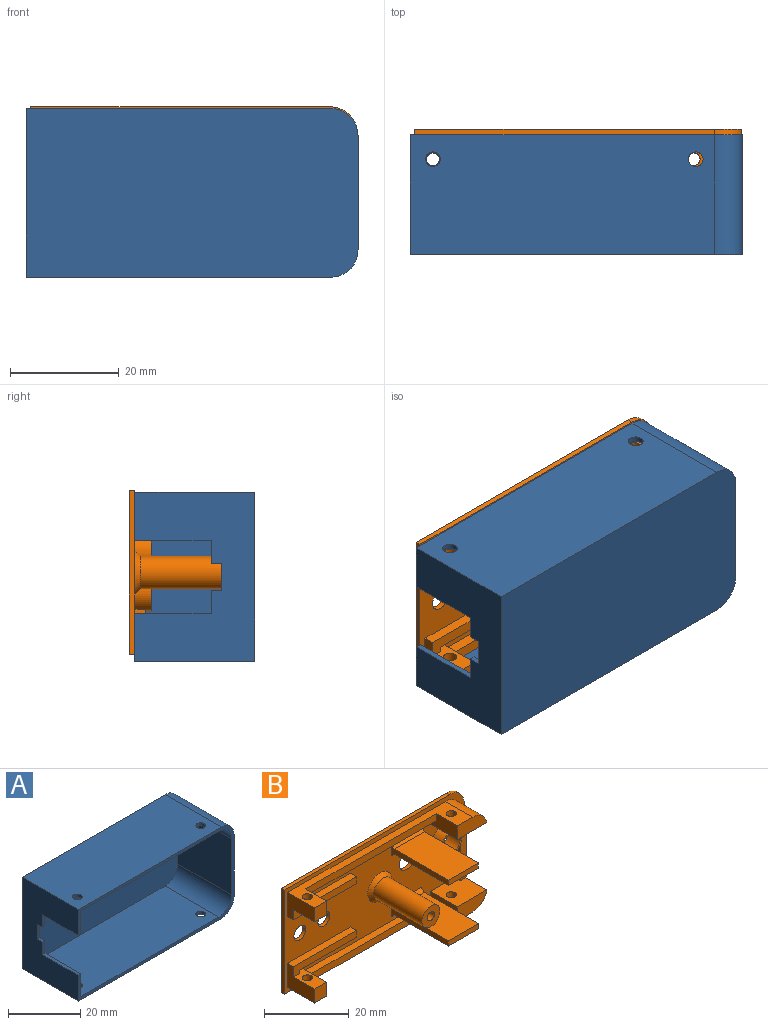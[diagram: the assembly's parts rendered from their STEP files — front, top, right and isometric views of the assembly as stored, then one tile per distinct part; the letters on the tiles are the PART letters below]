
ASSEMBLY  parts=2 mates=1
PART A: 26 faces, bbox 61x22x31 mm
  f0: plane 59x29mm, normal (0,-1,0), area 1700.3mm2, adj f8,f11,f12,f13,f14,f15
  f1: plane 56x22mm, normal (0,0,1), area 1220.5mm2, adj f2,f6,f7,f16,f19,f20
  f2: plane 31x22mm, normal (-1,0,0), area 483mm2, adj f1,f3,f7,f9,f10,f16,f21,f22
  f3: plane 56x22mm, normal (0,0,-1), area 1220.5mm2, adj f2,f4,f7,f16,f17,f18
  f4: cylinder r=5mm len=22mm, axis (0,1,0), area 172.8mm2, adj f3,f5,f7,f16
  f5: plane 22x21mm, normal (1,0,0), area 462mm2, adj f4,f6,f7,f16
  f6: cylinder r=5mm len=22mm, axis (0,1,0), area 172.8mm2, adj f1,f5,f7,f16
  f7: plane 61x31mm, normal (0,1,0), area 1880.3mm2, adj f1,f2,f3,f4,f5,f6
  f8: plane 29x21mm, normal (1,0,0), area 410mm2, adj f0,f9,f10,f11,f15,f16,f21,f22
  f9: plane 14x1mm, normal (0,0,1), area 14mm2, adj f2,f8,f16,f24
  f10: plane 14x1mm, normal (0,0,-1), area 14mm2, adj f2,f8,f16,f22
  f11: plane 54x21mm, normal (0,0,-1), area 1122.5mm2, adj f0,f8,f12,f16,f19,f20
  f12: cylinder r=5mm len=21mm, axis (0,1,0), area 164.9mm2, adj f0,f11,f13,f16
  f13: plane 21x19mm, normal (-1,0,0), area 399mm2, adj f0,f12,f14,f16
  f14: cylinder r=5mm len=21mm, axis (0,1,0), area 164.9mm2, adj f0,f13,f15,f16
  f15: plane 54x21mm, normal (0,0,1), area 1122.5mm2, adj f0,f8,f14,f16,f17,f18
  f16: plane 61x31mm, normal (0,-1,0), area 166.5mm2, adj f1,f2,f3,f4,f5,f6,f8,f9
  f17: cylinder r=1.35mm len=2.7mm, axis (0,0,-1), area 8.5mm2, adj f3,f15
  f18: cylinder r=1.35mm len=2.7mm, axis (0,0,-1), area 8.5mm2, adj f3,f15
  f19: cylinder r=1.35mm len=2.7mm, axis (0,0,-1), area 8.5mm2, adj f1,f11
  f20: cylinder r=1.35mm len=2.7mm, axis (0,0,-1), area 8.5mm2, adj f1,f11
  f21: plane 2x1mm, normal (0,0,-1), area 2mm2, adj f2,f8,f22,f25
  f22: plane 4.25x1mm, normal (0,-1,0), area 4.3mm2, adj f2,f8,f10,f21
  f23: plane 2x1mm, normal (0,0,1), area 2mm2, adj f2,f8,f24,f25
  f24: plane 4.25x1mm, normal (0,-1,0), area 4.3mm2, adj f2,f8,f9,f23
  f25: plane 5x1mm, normal (0,-1,0), area 5mm2, adj f2,f8,f21,f23
PART B: 75 faces, bbox 60x20x30 mm
  f0: plane 9x4mm, normal (1,0,0), area 32mm2, adj f1,f23,f25,f26,f56,f57
  f1: plane 60x30mm, normal (0,-1,0), area 1145.8mm2, adj f0,f2,f3,f4,f5,f6,f7,f8
  f2: plane 9x4mm, normal (0,0,1), area 27.5mm2, adj f1,f20,f21,f22,f52,f55,f69
  f3: plane 9x4mm, normal (-1,0,0), area 32mm2, adj f1,f16,f18,f19,f44,f45
  f4: plane 30x1mm, normal (-1,0,0), area 30mm2, adj f1,f5,f13,f15
  f5: plane 55x1mm, normal (0,0,-1), area 55mm2, adj f1,f4,f6,f15
  f6: cylinder r=5mm len=5mm, axis (0,1,0), area 7.9mm2, adj f1,f5,f7,f15
  f7: plane 20x1mm, normal (1,0,0), area 20mm2, adj f1,f6,f8,f15
  f8: cylinder r=5mm len=5mm, axis (0,1,0), area 7.9mm2, adj f1,f7,f13,f15
  f9: cylinder r=2.5mm len=5mm, axis (0,1,0), area 15.7mm2, adj f1,f15
  f10: cylinder r=2mm len=4mm, axis (0,1,0), area 12.6mm2, adj f1,f15
  f11: cylinder r=3mm len=6mm, axis (0,1,0), area 75.4mm2, adj f15,f63
  f12: cylinder r=2mm len=4mm, axis (0,1,0), area 12.6mm2, adj f1,f15
  f13: plane 55x1mm, normal (0,0,1), area 55mm2, adj f1,f4,f8,f15
  f14: cylinder r=3mm len=6mm, axis (0,1,0), area 75.4mm2, adj f15,f65
  f15: plane 60x30mm, normal (0,1,0), area 1688mm2, adj f4,f5,f6,f7,f8,f9,f10,f11
  f16: plane 52.4x9mm, normal (0,0,-1), area 158.8mm2, adj f1,f3,f17,f19,f20,f21,f22,f45
  f17: cylinder r=5mm len=9mm, axis (0,1,0), area 63.6mm2, adj f1,f16,f18,f19,f41,f43
  f18: plane 9.9x9mm, normal (0,0,1), area 80.8mm2, adj f1,f3,f17,f19,f42,f43,f68
  f19: plane 9.9x4mm, normal (0,-1,0), area 34.7mm2, adj f3,f16,f17,f18
  f20: plane 9x6.95mm, normal (-1,0,0), area 41.9mm2, adj f1,f2,f16,f22,f51,f55
  f21: plane 9x4mm, normal (1,0,0), area 32mm2, adj f1,f2,f16,f22,f44,f45
  f22: plane 4x4mm, normal (0,-1,0), area 16mm2, adj f2,f16,f20,f21
  f23: plane 52.4x9mm, normal (0,0,1), area 158.8mm2, adj f0,f1,f24,f26,f27,f29,f30,f57
  f24: plane 9x6.95mm, normal (-1,0,0), area 41.9mm2, adj f1,f23,f25,f26,f46,f50
  f25: plane 9x4mm, normal (0,0,-1), area 27.5mm2, adj f0,f1,f24,f26,f49,f50,f67
  f26: plane 4x4mm, normal (0,-1,0), area 16mm2, adj f0,f23,f24,f25
  f27: plane 9x4mm, normal (-1,0,0), area 32mm2, adj f1,f23,f28,f30,f56,f57
  f28: plane 9.9x9mm, normal (0,0,-1), area 80.8mm2, adj f1,f27,f29,f30,f42,f43,f66
  f29: cylinder r=5mm len=9mm, axis (0,1,0), area 63.6mm2, adj f1,f23,f28,f30,f41,f43
  f30: plane 9.9x4mm, normal (0,-1,0), area 34.7mm2, adj f23,f27,f28,f29
  f31: plane 18x10mm, normal (0,0,-1), area 180mm2, adj f32,f34,f35,f74
  f32: plane 19x3.5mm, normal (1,0,0), area 29.5mm2, adj f1,f31,f33,f35,f72,f74
  f33: plane 18x10mm, normal (0,0,1), area 180mm2, adj f32,f34,f35,f72
  f34: plane 19x3.5mm, normal (-1,0,0), area 29.5mm2, adj f1,f31,f33,f35,f72,f74
  f35: plane 10x1.5mm, normal (0,-1,0), area 15mm2, adj f31,f32,f33,f34
  f36: plane 19x3.5mm, normal (-1,0,0), area 29.5mm2, adj f1,f37,f39,f40,f71,f73
  f37: plane 18x10mm, normal (0,0,-1), area 180mm2, adj f36,f38,f40,f71
  f38: plane 19x3.5mm, normal (1,0,0), area 29.5mm2, adj f1,f37,f39,f40,f71,f73
  f39: plane 18x10mm, normal (0,0,1), area 180mm2, adj f36,f38,f40,f73
  f40: plane 10x1.5mm, normal (0,-1,0), area 15mm2, adj f36,f37,f38,f39
  f41: plane 17.4x2mm, normal (1,0,0), area 34.8mm2, adj f1,f17,f29,f43
  f42: plane 19.4x2mm, normal (-1,0,0), area 38.8mm2, adj f1,f18,f28,f43
  f43: plane 19.4x2mm, normal (0,-1,0), area 38.7mm2, adj f17,f18,f28,f29,f41,f42
  f44: plane 43.4x2mm, normal (0,0,1), area 86.8mm2, adj f1,f3,f21,f45
  f45: plane 43.4x2mm, normal (0,-1,0), area 86.8mm2, adj f3,f16,f21,f44
  f46: plane 21x2mm, normal (0,0,-1), area 42mm2, adj f1,f24,f47,f50
  f47: plane 2x2mm, normal (1,0,0), area 4mm2, adj f1,f46,f48,f50
  f48: plane 19x2mm, normal (0,0,1), area 38mm2, adj f1,f47,f49,f50
  f49: plane 2x0.95mm, normal (1,0,0), area 1.9mm2, adj f1,f25,f48,f50
  f50: plane 21x2.95mm, normal (0,-1,0), area 43.9mm2, adj f24,f25,f46,f47,f48,f49
  f51: plane 21x2mm, normal (0,0,1), area 42mm2, adj f1,f20,f54,f55
  f52: plane 2x0.95mm, normal (1,0,0), area 1.9mm2, adj f1,f2,f53,f55
  f53: plane 19x2mm, normal (0,0,-1), area 38mm2, adj f1,f52,f54,f55
  f54: plane 2x2mm, normal (1,0,0), area 4mm2, adj f1,f51,f53,f55
  f55: plane 21x2.95mm, normal (0,-1,0), area 43.9mm2, adj f2,f20,f51,f52,f53,f54
  f56: plane 43.4x2mm, normal (0,0,-1), area 86.8mm2, adj f0,f1,f27,f57
  f57: plane 43.4x2mm, normal (0,-1,0), area 86.8mm2, adj f0,f23,f27,f56
  f58: cylinder r=1.2mm len=17mm, axis (0,1,0), area 128.2mm2, adj f60,f61
  f59: cylinder r=3mm len=16mm, axis (0,1,0), area 301.6mm2, adj f60,f70
  f60: plane 6x6mm, normal (0,-1,0), area 23.8mm2, adj f58,f59
  f61: plane 2.4x2.4mm, normal (0,-1,0), area 4.5mm2, adj f58
  f62: cylinder r=3.5mm len=7mm, axis (0,1,0), area 66mm2, adj f1,f63
  f63: plane 7x7mm, normal (0,-1,0), area 10.2mm2, adj f11,f62
  f64: cylinder r=3.5mm len=7mm, axis (0,1,0), area 66mm2, adj f1,f65
  f65: plane 7x7mm, normal (0,-1,0), area 10.2mm2, adj f14,f64
  f66: cylinder r=1.2mm len=4mm, axis (0,0,-1), area 30.2mm2, adj f23,f28
  f67: cylinder r=1.2mm len=4mm, axis (0,0,-1), area 30.2mm2, adj f23,f25
  f68: cylinder r=1.2mm len=4mm, axis (0,0,-1), area 30.2mm2, adj f16,f18
  f69: cylinder r=1.2mm len=4mm, axis (0,0,-1), area 30.2mm2, adj f2,f16
  f70: cone r=4mm half-angle=45deg, axis (0,1,0), area 31.1mm2, adj f1,f59
  f71: plane 10x1mm, normal (0,-0.71,-0.71), area 14.1mm2, adj f1,f36,f37,f38
  f72: plane 10x1mm, normal (0,-0.71,0.71), area 14.1mm2, adj f1,f32,f33,f34
  f73: plane 10x1mm, normal (0,-0.71,0.71), area 14.1mm2, adj f1,f36,f38,f39
  f74: plane 10x1mm, normal (0,-0.71,-0.71), area 14.1mm2, adj f1,f31,f32,f34
PLACE A rot(axis=(1,0,0),180deg) t=(-18.33,-29.05,-4.82)mm
PLACE B t=(-17.93,-6.05,-4.02)mm
MATE fastened A.f17 <-> B.f67  axis (0,0,-1) through (-44.63,-11.55,9.68)mm
